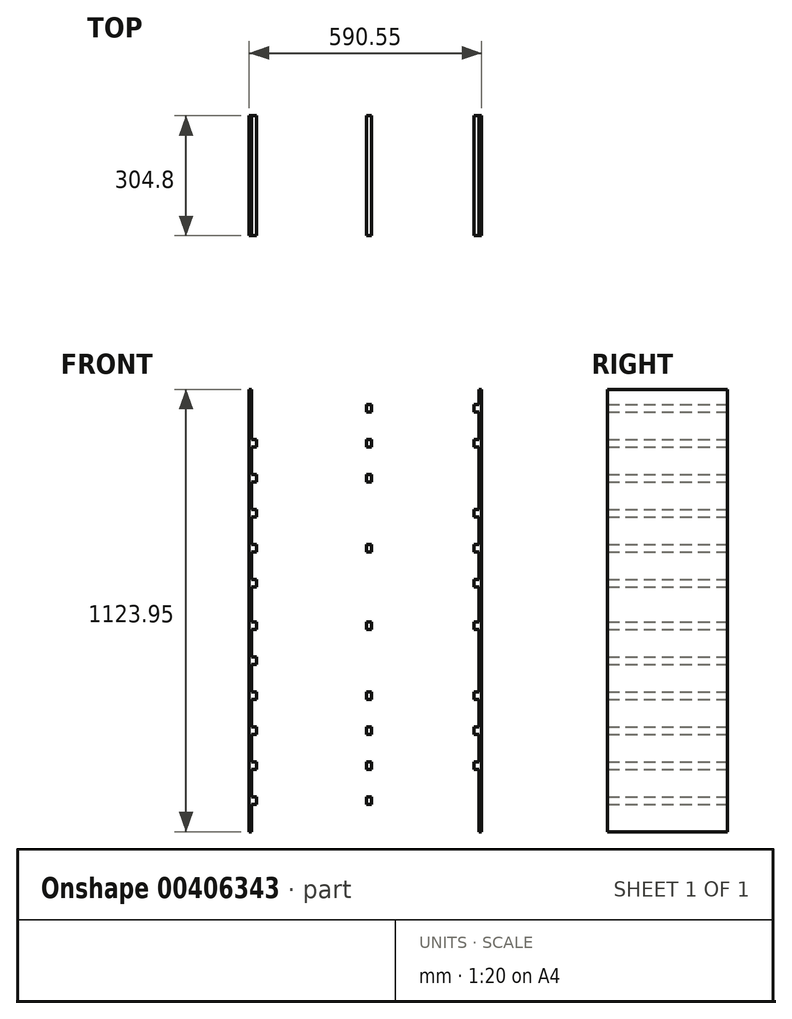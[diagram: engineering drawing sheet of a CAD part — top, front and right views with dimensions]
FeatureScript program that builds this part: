
annotation { "Feature Type Name" : "Feature", "Feature Type Description" : "" }
export const myFeature = defineFeature(function(context is Context, id is Id, definition is map)
    precondition{}
    {
        {
            var Q0;
            Q0=qCreatedBy(makeId("Front.planeOp"),FACE);
            var sketch = newSketch(context, id + "F0", { "sketchPlane" : qUnion([Q0])});
            skLineSegment(sketch, "E0.bottom", {"start": v(0, 0) * mm, "end": v(6.35, 0) * mm});
            skLineSegment(sketch, "E0.top", {"start": v(0, 1123.95) * mm, "end": v(6.35, 1123.95) * mm});
            skLineSegment(sketch, "E0.left", {"start": v(0, 0) * mm, "end": v(0, 1123.95) * mm});
            skLineSegment(sketch, "E0.right", {"start": v(6.35, 0) * mm, "end": v(6.35, 1123.95) * mm});
            skLineSegment(sketch, "E1.bottom", {"start": v(6.35, 0) * mm, "end": v(292.1, 0) * mm});
            skLineSegment(sketch, "E1.top", {"start": v(6.35, 19.05) * mm, "end": v(292.1, 19.05) * mm});
            skLineSegment(sketch, "E1.left", {"start": v(6.35, 0) * mm, "end": v(6.35, 19.05) * mm});
            skLineSegment(sketch, "E1.right", {"start": v(292.1, 0) * mm, "end": v(292.1, 19.05) * mm});
            skLineSegment(sketch, "E2.bottom", {"start": v(6.35, 69.85) * mm, "end": v(19.05, 69.85) * mm});
            skLineSegment(sketch, "E2.top", {"start": v(6.35, 88.9) * mm, "end": v(19.05, 88.9) * mm});
            skLineSegment(sketch, "E2.left", {"start": v(6.35, 69.85) * mm, "end": v(6.35, 88.9) * mm});
            skLineSegment(sketch, "E2.right", {"start": v(19.05, 69.85) * mm, "end": v(19.05, 88.9) * mm});
            skLineSegment(sketch, "E3.bottom", {"start": v(6.35, 158.75) * mm, "end": v(19.05, 158.75) * mm});
            skLineSegment(sketch, "E3.top", {"start": v(6.35, 177.8) * mm, "end": v(19.05, 177.8) * mm});
            skLineSegment(sketch, "E3.left", {"start": v(6.35, 158.75) * mm, "end": v(6.35, 177.8) * mm});
            skLineSegment(sketch, "E3.right", {"start": v(19.05, 158.75) * mm, "end": v(19.05, 177.8) * mm});
            skLineSegment(sketch, "E4.bottom", {"start": v(6.35, 247.65) * mm, "end": v(19.05, 247.65) * mm});
            skLineSegment(sketch, "E4.top", {"start": v(6.35, 266.7) * mm, "end": v(19.05, 266.7) * mm});
            skLineSegment(sketch, "E4.left", {"start": v(6.35, 247.65) * mm, "end": v(6.35, 266.7) * mm});
            skLineSegment(sketch, "E4.right", {"start": v(19.05, 247.65) * mm, "end": v(19.05, 266.7) * mm});
            skLineSegment(sketch, "E5.bottom", {"start": v(6.35, 336.55) * mm, "end": v(19.05, 336.55) * mm});
            skLineSegment(sketch, "E5.top", {"start": v(6.35, 355.6) * mm, "end": v(19.05, 355.6) * mm});
            skLineSegment(sketch, "E5.left", {"start": v(6.35, 336.55) * mm, "end": v(6.35, 355.6) * mm});
            skLineSegment(sketch, "E5.right", {"start": v(19.05, 336.55) * mm, "end": v(19.05, 355.6) * mm});
            skLineSegment(sketch, "E6.bottom", {"start": v(6.35, 425.45) * mm, "end": v(19.05, 425.45) * mm});
            skLineSegment(sketch, "E6.top", {"start": v(6.35, 444.5) * mm, "end": v(19.05, 444.5) * mm});
            skLineSegment(sketch, "E6.left", {"start": v(6.35, 425.45) * mm, "end": v(6.35, 444.5) * mm});
            skLineSegment(sketch, "E6.right", {"start": v(19.05, 425.45) * mm, "end": v(19.05, 444.5) * mm});
            skLineSegment(sketch, "E7.bottom", {"start": v(6.35, 514.35) * mm, "end": v(19.05, 514.35) * mm});
            skLineSegment(sketch, "E7.top", {"start": v(6.35, 533.4) * mm, "end": v(19.05, 533.4) * mm});
            skLineSegment(sketch, "E7.left", {"start": v(6.35, 514.35) * mm, "end": v(6.35, 533.4) * mm});
            skLineSegment(sketch, "E7.right", {"start": v(19.05, 514.35) * mm, "end": v(19.05, 533.4) * mm});
            skLineSegment(sketch, "E8.bottom", {"start": v(6.35, 571.5) * mm, "end": v(292.1, 571.5) * mm});
            skLineSegment(sketch, "E8.top", {"start": v(6.35, 552.45) * mm, "end": v(292.1, 552.45) * mm});
            skLineSegment(sketch, "E8.left", {"start": v(6.35, 571.5) * mm, "end": v(6.35, 552.45) * mm});
            skLineSegment(sketch, "E8.right", {"start": v(292.1, 571.5) * mm, "end": v(292.1, 552.45) * mm});
            skLineSegment(sketch, "E9.0.1.0", {"start": v(6.35, 1123.95) * mm, "end": v(292.1, 1123.95) * mm});
            skLineSegment(sketch, "E9.0.1.1", {"start": v(6.35, 1104.9) * mm, "end": v(292.1, 1104.9) * mm});
            skLineSegment(sketch, "E9.0.1.2", {"start": v(6.35, 908.05) * mm, "end": v(19.05, 908.05) * mm});
            skLineSegment(sketch, "E9.0.1.3", {"start": v(6.35, 819.15) * mm, "end": v(19.05, 819.15) * mm});
            skLineSegment(sketch, "E9.0.1.4", {"start": v(6.35, 1066.8) * mm, "end": v(6.35, 1085.85) * mm});
            skLineSegment(sketch, "E9.0.1.5", {"start": v(6.35, 622.3) * mm, "end": v(19.05, 622.3) * mm});
            skLineSegment(sketch, "E9.0.1.6", {"start": v(6.35, 641.35) * mm, "end": v(19.05, 641.35) * mm});
            skLineSegment(sketch, "E9.0.1.7", {"start": v(6.35, 622.3) * mm, "end": v(6.35, 641.35) * mm});
            skLineSegment(sketch, "E9.0.1.8", {"start": v(6.35, 977.9) * mm, "end": v(19.05, 977.9) * mm});
            skLineSegment(sketch, "E9.0.1.9", {"start": v(6.35, 1066.8) * mm, "end": v(19.05, 1066.8) * mm});
            skLineSegment(sketch, "E9.0.1.10", {"start": v(19.05, 622.3) * mm, "end": v(19.05, 641.35) * mm});
            skLineSegment(sketch, "E9.0.1.11", {"start": v(6.35, 711.2) * mm, "end": v(19.05, 711.2) * mm});
            skLineSegment(sketch, "E9.0.1.12", {"start": v(19.05, 977.9) * mm, "end": v(19.05, 996.95) * mm});
            skLineSegment(sketch, "E9.0.1.13", {"start": v(19.05, 889) * mm, "end": v(19.05, 908.05) * mm});
            skLineSegment(sketch, "E9.0.1.14", {"start": v(6.35, 889) * mm, "end": v(19.05, 889) * mm});
            skLineSegment(sketch, "E9.0.1.15", {"start": v(19.05, 711.2) * mm, "end": v(19.05, 730.25) * mm});
            skLineSegment(sketch, "E9.0.1.16", {"start": v(6.35, 1085.85) * mm, "end": v(19.05, 1085.85) * mm});
            skLineSegment(sketch, "E9.0.1.17", {"start": v(6.35, 800.1) * mm, "end": v(19.05, 800.1) * mm});
            skLineSegment(sketch, "E9.0.1.18", {"start": v(6.35, 730.25) * mm, "end": v(19.05, 730.25) * mm});
            skLineSegment(sketch, "E9.0.1.19", {"start": v(6.35, 711.2) * mm, "end": v(6.35, 730.25) * mm});
            skLineSegment(sketch, "E9.0.1.20", {"start": v(292.1, 1123.95) * mm, "end": v(292.1, 1104.9) * mm});
            skLineSegment(sketch, "E9.0.1.21", {"start": v(19.05, 800.1) * mm, "end": v(19.05, 819.15) * mm});
            skLineSegment(sketch, "E9.0.1.22", {"start": v(6.35, 977.9) * mm, "end": v(6.35, 996.95) * mm});
            skLineSegment(sketch, "E9.0.1.23", {"start": v(6.35, 996.95) * mm, "end": v(19.05, 996.95) * mm});
            skLineSegment(sketch, "E9.0.1.24", {"start": v(6.35, 889) * mm, "end": v(6.35, 908.05) * mm});
            skLineSegment(sketch, "E9.0.1.25", {"start": v(19.05, 1066.8) * mm, "end": v(19.05, 1085.85) * mm});
            skLineSegment(sketch, "E9.0.1.26", {"start": v(6.35, 800.1) * mm, "end": v(6.35, 819.15) * mm});
            skLineSegment(sketch, "E9.0.1.27", {"start": v(6.35, 1123.95) * mm, "end": v(6.35, 1104.9) * mm});
            skLineSegment(sketch, "E9.direction1", {"start": v(6.35, 69.85) * mm, "end": v(43.2, 69.85) * mm, "construction": true});
            skLineSegment(sketch, "E9.direction2", {"start": v(6.35, 69.85) * mm, "end": v(6.35, 622.3) * mm, "construction": true});
            skLineSegment(sketch, "E10.1.0.0", {"start": v(298.45, 1123.95) * mm, "end": v(584.2, 1123.95) * mm});
            skLineSegment(sketch, "E10.1.0.1", {"start": v(298.45, 1104.9) * mm, "end": v(584.2, 1104.9) * mm});
            skLineSegment(sketch, "E10.1.0.2", {"start": v(298.45, 0) * mm, "end": v(298.45, 1123.95) * mm});
            skLineSegment(sketch, "E10.1.0.3", {"start": v(292.1, 0) * mm, "end": v(292.1, 1123.95) * mm});
            skLineSegment(sketch, "E10.1.0.4", {"start": v(298.45, 0) * mm, "end": v(584.2, 0) * mm});
            skLineSegment(sketch, "E10.1.0.5", {"start": v(298.45, 19.05) * mm, "end": v(584.2, 19.05) * mm});
            skLineSegment(sketch, "E10.1.0.6", {"start": v(298.45, 571.5) * mm, "end": v(584.2, 571.5) * mm});
            skLineSegment(sketch, "E10.1.0.7", {"start": v(298.45, 69.85) * mm, "end": v(298.45, 622.3) * mm, "construction": true});
            skLineSegment(sketch, "E10.1.0.8", {"start": v(298.45, 552.45) * mm, "end": v(584.2, 552.45) * mm});
            skLineSegment(sketch, "E10.1.0.9", {"start": v(298.45, 69.85) * mm, "end": v(335.3, 69.85) * mm, "construction": true});
            skLineSegment(sketch, "E10.1.0.10", {"start": v(298.45, 425.45) * mm, "end": v(298.45, 444.5) * mm});
            skLineSegment(sketch, "E10.1.0.11", {"start": v(298.45, 1085.85) * mm, "end": v(311.15, 1085.85) * mm});
            skLineSegment(sketch, "E10.1.0.12", {"start": v(298.45, 1066.8) * mm, "end": v(311.15, 1066.8) * mm});
            skLineSegment(sketch, "E10.1.0.13", {"start": v(298.45, 177.8) * mm, "end": v(311.15, 177.8) * mm});
            skLineSegment(sketch, "E10.1.0.14", {"start": v(298.45, 908.05) * mm, "end": v(311.15, 908.05) * mm});
            skLineSegment(sketch, "E10.1.0.15", {"start": v(298.45, 158.75) * mm, "end": v(298.45, 177.8) * mm});
            skLineSegment(sketch, "E10.1.0.16", {"start": v(311.15, 514.35) * mm, "end": v(311.15, 533.4) * mm});
            skLineSegment(sketch, "E10.1.0.17", {"start": v(311.15, 1066.8) * mm, "end": v(311.15, 1085.85) * mm});
            skLineSegment(sketch, "E10.1.0.18", {"start": v(311.15, 425.45) * mm, "end": v(311.15, 444.5) * mm});
            skLineSegment(sketch, "E10.1.0.19", {"start": v(298.45, 336.55) * mm, "end": v(311.15, 336.55) * mm});
            skLineSegment(sketch, "E10.1.0.20", {"start": v(298.45, 622.3) * mm, "end": v(298.45, 641.35) * mm});
            skLineSegment(sketch, "E10.1.0.21", {"start": v(298.45, 996.95) * mm, "end": v(311.15, 996.95) * mm});
            skLineSegment(sketch, "E10.1.0.22", {"start": v(298.45, 514.35) * mm, "end": v(298.45, 533.4) * mm});
            skLineSegment(sketch, "E10.1.0.23", {"start": v(311.15, 158.75) * mm, "end": v(311.15, 177.8) * mm});
            skLineSegment(sketch, "E10.1.0.24", {"start": v(311.15, 711.2) * mm, "end": v(311.15, 730.25) * mm});
            skLineSegment(sketch, "E10.1.0.25", {"start": v(584.2, 571.5) * mm, "end": v(584.2, 552.45) * mm});
            skLineSegment(sketch, "E10.1.0.26", {"start": v(298.45, 711.2) * mm, "end": v(311.15, 711.2) * mm});
            skLineSegment(sketch, "E10.1.0.27", {"start": v(298.45, 1123.95) * mm, "end": v(298.45, 1104.9) * mm});
            skLineSegment(sketch, "E10.1.0.28", {"start": v(298.45, 730.25) * mm, "end": v(311.15, 730.25) * mm});
            skLineSegment(sketch, "E10.1.0.29", {"start": v(298.45, 889) * mm, "end": v(298.45, 908.05) * mm});
            skLineSegment(sketch, "E10.1.0.30", {"start": v(298.45, 977.9) * mm, "end": v(311.15, 977.9) * mm});
            skLineSegment(sketch, "E10.1.0.31", {"start": v(298.45, 355.6) * mm, "end": v(311.15, 355.6) * mm});
            skLineSegment(sketch, "E10.1.0.32", {"start": v(298.45, 336.55) * mm, "end": v(298.45, 355.6) * mm});
            skLineSegment(sketch, "E10.1.0.33", {"start": v(311.15, 622.3) * mm, "end": v(311.15, 641.35) * mm});
            skLineSegment(sketch, "E10.1.0.34", {"start": v(298.45, 514.35) * mm, "end": v(311.15, 514.35) * mm});
            skLineSegment(sketch, "E10.1.0.35", {"start": v(298.45, 800.1) * mm, "end": v(298.45, 819.15) * mm});
            skLineSegment(sketch, "E10.1.0.36", {"start": v(298.45, 800.1) * mm, "end": v(311.15, 800.1) * mm});
            skLineSegment(sketch, "E10.1.0.37", {"start": v(298.45, 641.35) * mm, "end": v(311.15, 641.35) * mm});
            skLineSegment(sketch, "E10.1.0.38", {"start": v(298.45, 977.9) * mm, "end": v(298.45, 996.95) * mm});
            skLineSegment(sketch, "E10.1.0.39", {"start": v(584.2, 0) * mm, "end": v(584.2, 19.05) * mm});
            skLineSegment(sketch, "E10.1.0.40", {"start": v(298.45, 88.9) * mm, "end": v(311.15, 88.9) * mm});
            skLineSegment(sketch, "E10.1.0.41", {"start": v(298.45, 69.85) * mm, "end": v(298.45, 88.9) * mm});
            skLineSegment(sketch, "E10.1.0.42", {"start": v(311.15, 69.85) * mm, "end": v(311.15, 88.9) * mm});
            skLineSegment(sketch, "E10.1.0.43", {"start": v(298.45, 158.75) * mm, "end": v(311.15, 158.75) * mm});
            skLineSegment(sketch, "E10.1.0.44", {"start": v(298.45, 711.2) * mm, "end": v(298.45, 730.25) * mm});
            skLineSegment(sketch, "E10.1.0.45", {"start": v(298.45, 819.15) * mm, "end": v(311.15, 819.15) * mm});
            skLineSegment(sketch, "E10.1.0.46", {"start": v(311.15, 336.55) * mm, "end": v(311.15, 355.6) * mm});
            skLineSegment(sketch, "E10.1.0.47", {"start": v(298.45, 247.65) * mm, "end": v(311.15, 247.65) * mm});
            skLineSegment(sketch, "E10.1.0.48", {"start": v(311.15, 977.9) * mm, "end": v(311.15, 996.95) * mm});
            skLineSegment(sketch, "E10.1.0.49", {"start": v(584.2, 1123.95) * mm, "end": v(584.2, 1104.9) * mm});
            skLineSegment(sketch, "E10.1.0.50", {"start": v(298.45, 1066.8) * mm, "end": v(298.45, 1085.85) * mm});
            skLineSegment(sketch, "E10.1.0.51", {"start": v(298.45, 425.45) * mm, "end": v(311.15, 425.45) * mm});
            skLineSegment(sketch, "E10.1.0.52", {"start": v(311.15, 889) * mm, "end": v(311.15, 908.05) * mm});
            skLineSegment(sketch, "E10.1.0.53", {"start": v(311.15, 800.1) * mm, "end": v(311.15, 819.15) * mm});
            skLineSegment(sketch, "E10.1.0.54", {"start": v(298.45, 444.5) * mm, "end": v(311.15, 444.5) * mm});
            skLineSegment(sketch, "E10.1.0.55", {"start": v(298.45, 247.65) * mm, "end": v(298.45, 266.7) * mm});
            skLineSegment(sketch, "E10.1.0.56", {"start": v(298.45, 889) * mm, "end": v(311.15, 889) * mm});
            skLineSegment(sketch, "E10.1.0.57", {"start": v(298.45, 571.5) * mm, "end": v(298.45, 552.45) * mm});
            skLineSegment(sketch, "E10.1.0.58", {"start": v(311.15, 247.65) * mm, "end": v(311.15, 266.7) * mm});
            skLineSegment(sketch, "E10.1.0.59", {"start": v(298.45, 266.7) * mm, "end": v(311.15, 266.7) * mm});
            skLineSegment(sketch, "E10.1.0.60", {"start": v(298.45, 622.3) * mm, "end": v(311.15, 622.3) * mm});
            skLineSegment(sketch, "E10.1.0.61", {"start": v(298.45, 533.4) * mm, "end": v(311.15, 533.4) * mm});
            skLineSegment(sketch, "E10.1.0.62", {"start": v(292.1, 0) * mm, "end": v(298.45, 0) * mm});
            skLineSegment(sketch, "E10.1.0.63", {"start": v(292.1, 1123.95) * mm, "end": v(298.45, 1123.95) * mm});
            skLineSegment(sketch, "E10.1.0.64", {"start": v(298.45, 0) * mm, "end": v(298.45, 19.05) * mm});
            skLineSegment(sketch, "E10.1.0.65", {"start": v(298.45, 69.85) * mm, "end": v(311.15, 69.85) * mm});
            skLineSegment(sketch, "E10.direction1", {"start": v(0, 0) * mm, "end": v(292.1, 0) * mm, "construction": true});
            skLineSegment(sketch, "E11.bottom", {"start": v(584.2, 0) * mm, "end": v(590.55, 0) * mm});
            skLineSegment(sketch, "E11.top", {"start": v(584.2, 1123.95) * mm, "end": v(590.55, 1123.95) * mm});
            skLineSegment(sketch, "E11.left", {"start": v(584.2, 0) * mm, "end": v(584.2, 1123.95) * mm});
            skLineSegment(sketch, "E11.right", {"start": v(590.55, 0) * mm, "end": v(590.55, 1123.95) * mm});
            skLineSegment(sketch, "E12.1.0.0", {"start": v(584.2, 69.85) * mm, "end": v(584.2, 88.9) * mm});
            skLineSegment(sketch, "E12.1.0.1", {"start": v(571.5, 69.85) * mm, "end": v(571.5, 622.3) * mm, "construction": true});
            skLineSegment(sketch, "E12.1.0.2", {"start": v(571.5, 336.55) * mm, "end": v(571.5, 355.6) * mm});
            skLineSegment(sketch, "E12.1.0.3", {"start": v(571.5, 336.55) * mm, "end": v(584.2, 336.55) * mm});
            skLineSegment(sketch, "E12.1.0.4", {"start": v(571.5, 977.9) * mm, "end": v(584.2, 977.9) * mm});
            skLineSegment(sketch, "E12.1.0.5", {"start": v(584.2, 336.55) * mm, "end": v(584.2, 355.6) * mm});
            skLineSegment(sketch, "E12.1.0.6", {"start": v(571.5, 514.35) * mm, "end": v(584.2, 514.35) * mm});
            skLineSegment(sketch, "E12.1.0.7", {"start": v(571.5, 1066.8) * mm, "end": v(571.5, 1085.85) * mm});
            skLineSegment(sketch, "E12.1.0.8", {"start": v(584.2, 425.45) * mm, "end": v(584.2, 444.5) * mm});
            skLineSegment(sketch, "E12.1.0.9", {"start": v(571.5, 800.1) * mm, "end": v(571.5, 819.15) * mm});
            skLineSegment(sketch, "E12.1.0.10", {"start": v(571.5, 425.45) * mm, "end": v(584.2, 425.45) * mm});
            skLineSegment(sketch, "E12.1.0.11", {"start": v(584.2, 977.9) * mm, "end": v(584.2, 996.95) * mm});
            skLineSegment(sketch, "E12.1.0.12", {"start": v(584.2, 889) * mm, "end": v(584.2, 908.05) * mm});
            skLineSegment(sketch, "E12.1.0.13", {"start": v(571.5, 800.1) * mm, "end": v(584.2, 800.1) * mm});
            skLineSegment(sketch, "E12.1.0.14", {"start": v(571.5, 908.05) * mm, "end": v(584.2, 908.05) * mm});
            skLineSegment(sketch, "E12.1.0.15", {"start": v(584.2, 800.1) * mm, "end": v(584.2, 819.15) * mm});
            skLineSegment(sketch, "E12.1.0.16", {"start": v(571.5, 641.35) * mm, "end": v(584.2, 641.35) * mm});
            skLineSegment(sketch, "E12.1.0.17", {"start": v(571.5, 996.95) * mm, "end": v(584.2, 996.95) * mm});
            skLineSegment(sketch, "E12.1.0.18", {"start": v(584.2, 1066.8) * mm, "end": v(584.2, 1085.85) * mm});
            skLineSegment(sketch, "E12.1.0.19", {"start": v(565.15, 571.5) * mm, "end": v(565.15, 552.45) * mm});
            skLineSegment(sketch, "E12.1.0.20", {"start": v(584.2, 622.3) * mm, "end": v(584.2, 641.35) * mm});
            skLineSegment(sketch, "E12.1.0.21", {"start": v(571.5, 889) * mm, "end": v(571.5, 908.05) * mm});
            skLineSegment(sketch, "E12.1.0.22", {"start": v(571.5, 819.15) * mm, "end": v(584.2, 819.15) * mm});
            skLineSegment(sketch, "E12.1.0.23", {"start": v(571.5, 533.4) * mm, "end": v(584.2, 533.4) * mm});
            skLineSegment(sketch, "E12.1.0.24", {"start": v(571.5, 177.8) * mm, "end": v(584.2, 177.8) * mm});
            skLineSegment(sketch, "E12.1.0.25", {"start": v(571.5, 730.25) * mm, "end": v(584.2, 730.25) * mm});
            skLineSegment(sketch, "E12.1.0.26", {"start": v(571.5, 711.2) * mm, "end": v(571.5, 730.25) * mm});
            skLineSegment(sketch, "E12.1.0.27", {"start": v(571.5, 444.5) * mm, "end": v(584.2, 444.5) * mm});
            skLineSegment(sketch, "E12.1.0.28", {"start": v(571.5, 977.9) * mm, "end": v(571.5, 996.95) * mm});
            skLineSegment(sketch, "E12.1.0.29", {"start": v(571.5, 514.35) * mm, "end": v(571.5, 533.4) * mm});
            skLineSegment(sketch, "E12.1.0.30", {"start": v(571.5, 247.65) * mm, "end": v(571.5, 266.7) * mm});
            skLineSegment(sketch, "E12.1.0.31", {"start": v(584.2, 158.75) * mm, "end": v(584.2, 177.8) * mm});
            skLineSegment(sketch, "E12.1.0.32", {"start": v(571.5, 158.75) * mm, "end": v(571.5, 177.8) * mm});
            skLineSegment(sketch, "E12.1.0.33", {"start": v(571.5, 889) * mm, "end": v(584.2, 889) * mm});
            skLineSegment(sketch, "E12.1.0.34", {"start": v(571.5, 88.9) * mm, "end": v(584.2, 88.9) * mm});
            skLineSegment(sketch, "E12.1.0.35", {"start": v(584.2, 711.2) * mm, "end": v(584.2, 730.25) * mm});
            skLineSegment(sketch, "E12.1.0.36", {"start": v(571.5, 247.65) * mm, "end": v(584.2, 247.65) * mm});
            skLineSegment(sketch, "E12.1.0.37", {"start": v(571.5, 355.6) * mm, "end": v(584.2, 355.6) * mm});
            skLineSegment(sketch, "E12.1.0.38", {"start": v(571.5, 571.5) * mm, "end": v(571.5, 552.45) * mm});
            skLineSegment(sketch, "E12.1.0.39", {"start": v(571.5, 69.85) * mm, "end": v(571.5, 88.9) * mm});
            skLineSegment(sketch, "E12.1.0.40", {"start": v(571.5, 1085.85) * mm, "end": v(584.2, 1085.85) * mm});
            skLineSegment(sketch, "E12.1.0.41", {"start": v(571.5, 266.7) * mm, "end": v(584.2, 266.7) * mm});
            skLineSegment(sketch, "E12.1.0.42", {"start": v(571.5, 158.75) * mm, "end": v(584.2, 158.75) * mm});
            skLineSegment(sketch, "E12.1.0.43", {"start": v(584.2, 247.65) * mm, "end": v(584.2, 266.7) * mm});
            skLineSegment(sketch, "E12.1.0.44", {"start": v(584.2, 514.35) * mm, "end": v(584.2, 533.4) * mm});
            skLineSegment(sketch, "E12.1.0.45", {"start": v(571.5, 711.2) * mm, "end": v(584.2, 711.2) * mm});
            skLineSegment(sketch, "E12.1.0.46", {"start": v(571.5, 425.45) * mm, "end": v(571.5, 444.5) * mm});
            skLineSegment(sketch, "E12.1.0.47", {"start": v(571.5, 1066.8) * mm, "end": v(584.2, 1066.8) * mm});
            skLineSegment(sketch, "E12.1.0.48", {"start": v(571.5, 622.3) * mm, "end": v(571.5, 641.35) * mm});
            skLineSegment(sketch, "E12.1.0.49", {"start": v(571.5, 622.3) * mm, "end": v(584.2, 622.3) * mm});
            skLineSegment(sketch, "E12.1.0.50", {"start": v(571.5, 69.85) * mm, "end": v(584.2, 69.85) * mm});
            skLineSegment(sketch, "E12.direction1", {"start": v(298.45, 69.85) * mm, "end": v(571.5, 69.85) * mm, "construction": true});
            skSolve(sketch);
        }
        {
            var Q0;
            Q0=makeQuery(id+"F0.imprint","IMPRINT",FACE,{"disambiguationData":[TD([[makeQuery(id+"F0.imprint","IMPRINT",EDGE,{"derivedFrom":sQuery(id+"F0.wireOp",EDGE,"E2.bottom")}),1.0]])]});
            var Q1;
            Q1=makeQuery(id+"F0.imprint","IMPRINT",FACE,{"disambiguationData":[TD([[makeQuery(id+"F0.imprint","IMPRINT",EDGE,{"derivedFrom":sQuery(id+"F0.wireOp",EDGE,"E3.bottom")}),1.0]])]});
            var Q2;
            Q2=makeQuery(id+"F0.imprint","IMPRINT",FACE,{"disambiguationData":[TD([[makeQuery(id+"F0.imprint","IMPRINT",EDGE,{"derivedFrom":sQuery(id+"F0.wireOp",EDGE,"E4.bottom")}),1.0]])]});
            var Q3;
            Q3=makeQuery(id+"F0.imprint","IMPRINT",FACE,{"disambiguationData":[TD([[makeQuery(id+"F0.imprint","IMPRINT",EDGE,{"derivedFrom":sQuery(id+"F0.wireOp",EDGE,"E5.bottom")}),1.0]])]});
            var Q4;
            Q4=makeQuery(id+"F0.imprint","IMPRINT",FACE,{"disambiguationData":[TD([[makeQuery(id+"F0.imprint","IMPRINT",EDGE,{"derivedFrom":sQuery(id+"F0.wireOp",EDGE,"E6.bottom")}),1.0]])]});
            var Q5;
            Q5=makeQuery(id+"F0.imprint","IMPRINT",FACE,{"disambiguationData":[TD([[makeQuery(id+"F0.imprint","IMPRINT",EDGE,{"derivedFrom":sQuery(id+"F0.wireOp",EDGE,"E7.bottom")}),1.0]])]});
            var Q6;
            Q6=makeQuery(id+"F0.imprint","IMPRINT",FACE,{"disambiguationData":[TD([[makeQuery(id+"F0.imprint","IMPRINT",EDGE,{"derivedFrom":sQuery(id+"F0.wireOp",EDGE,"E9.0.1.2")}),-1.0]])]});
            var Q7;
            Q7=makeQuery(id+"F0.imprint","IMPRINT",FACE,{"disambiguationData":[TD([[makeQuery(id+"F0.imprint","IMPRINT",EDGE,{"derivedFrom":sQuery(id+"F0.wireOp",EDGE,"E9.0.1.3")}),-1.0]])]});
            var Q8;
            Q8=makeQuery(id+"F0.imprint","IMPRINT",FACE,{"disambiguationData":[TD([[makeQuery(id+"F0.imprint","IMPRINT",EDGE,{"derivedFrom":sQuery(id+"F0.wireOp",EDGE,"E9.0.1.4")}),-1.0]])]});
            var Q9;
            Q9=makeQuery(id+"F0.imprint","IMPRINT",FACE,{"disambiguationData":[TD([[makeQuery(id+"F0.imprint","IMPRINT",EDGE,{"derivedFrom":sQuery(id+"F0.wireOp",EDGE,"E9.0.1.5")}),1.0]])]});
            var Q10;
            Q10=makeQuery(id+"F0.imprint","IMPRINT",FACE,{"disambiguationData":[TD([[makeQuery(id+"F0.imprint","IMPRINT",EDGE,{"derivedFrom":sQuery(id+"F0.wireOp",EDGE,"E9.0.1.8")}),1.0]])]});
            var Q11;
            Q11=makeQuery(id+"F0.imprint","IMPRINT",FACE,{"disambiguationData":[TD([[makeQuery(id+"F0.imprint","IMPRINT",EDGE,{"derivedFrom":sQuery(id+"F0.wireOp",EDGE,"E9.0.1.11")}),1.0]])]});
            var Q12;
            Q12=makeQuery(id+"F0.imprint","IMPRINT",FACE,{"disambiguationData":[TD([[makeQuery(id+"F0.imprint","IMPRINT",EDGE,{"derivedFrom":sQuery(id+"F0.wireOp",EDGE,"E12.1.0.9")}),-1.0]])]});
            var Q13;
            Q13=makeQuery(id+"F0.imprint","IMPRINT",FACE,{"disambiguationData":[TD([[makeQuery(id+"F0.imprint","IMPRINT",EDGE,{"derivedFrom":sQuery(id+"F0.wireOp",EDGE,"E10.1.0.35")}),-1.0]])]});
            var Q14;
            Q14=makeQuery(id+"F0.imprint","IMPRINT",FACE,{"disambiguationData":[TD([[makeQuery(id+"F0.imprint","IMPRINT",EDGE,{"derivedFrom":sQuery(id+"F0.wireOp",EDGE,"E12.1.0.7")}),-1.0]])]});
            var Q15;
            Q15=makeQuery(id+"F0.imprint","IMPRINT",FACE,{"disambiguationData":[TD([[makeQuery(id+"F0.imprint","IMPRINT",EDGE,{"derivedFrom":sQuery(id+"F0.wireOp",EDGE,"E10.1.0.14")}),-1.0]])]});
            var Q16;
            Q16=makeQuery(id+"F0.imprint","IMPRINT",FACE,{"disambiguationData":[TD([[makeQuery(id+"F0.imprint","IMPRINT",EDGE,{"derivedFrom":sQuery(id+"F0.wireOp",EDGE,"E10.1.0.11")}),-1.0]])]});
            var Q17;
            Q17=makeQuery(id+"F0.imprint","IMPRINT",FACE,{"disambiguationData":[TD([[makeQuery(id+"F0.imprint","IMPRINT",EDGE,{"derivedFrom":sQuery(id+"F0.wireOp",EDGE,"E12.1.0.16")}),-1.0]])]});
            var Q18;
            Q18=makeQuery(id+"F0.imprint","IMPRINT",FACE,{"disambiguationData":[TD([[makeQuery(id+"F0.imprint","IMPRINT",EDGE,{"derivedFrom":sQuery(id+"F0.wireOp",EDGE,"E12.1.0.12")}),1.0]])]});
            var Q19;
            Q19=makeQuery(id+"F0.imprint","IMPRINT",FACE,{"disambiguationData":[TD([[makeQuery(id+"F0.imprint","IMPRINT",EDGE,{"derivedFrom":sQuery(id+"F0.wireOp",EDGE,"E10.1.0.24")}),1.0]])]});
            var Q20;
            Q20=makeQuery(id+"F0.imprint","IMPRINT",FACE,{"disambiguationData":[TD([[makeQuery(id+"F0.imprint","IMPRINT",EDGE,{"derivedFrom":sQuery(id+"F0.wireOp",EDGE,"E10.1.0.21")}),-1.0]])]});
            var Q21;
            Q21=makeQuery(id+"F0.imprint","IMPRINT",FACE,{"disambiguationData":[TD([[makeQuery(id+"F0.imprint","IMPRINT",EDGE,{"derivedFrom":sQuery(id+"F0.wireOp",EDGE,"E12.1.0.25")}),-1.0]])]});
            var Q22;
            Q22=makeQuery(id+"F0.imprint","IMPRINT",FACE,{"disambiguationData":[TD([[makeQuery(id+"F0.imprint","IMPRINT",EDGE,{"derivedFrom":sQuery(id+"F0.wireOp",EDGE,"E12.1.0.4")}),1.0]])]});
            var Q23;
            Q23=makeQuery(id+"F0.imprint","IMPRINT",FACE,{"disambiguationData":[TD([[makeQuery(id+"F0.imprint","IMPRINT",EDGE,{"derivedFrom":sQuery(id+"F0.wireOp",EDGE,"E10.1.0.20")}),-1.0]])]});
            var Q24;
            Q24=makeQuery(id+"F0.imprint","IMPRINT",FACE,{"disambiguationData":[TD([[makeQuery(id+"F0.imprint","IMPRINT",EDGE,{"derivedFrom":sQuery(id+"F0.wireOp",EDGE,"E12.1.0.8")}),1.0]])]});
            var Q25;
            Q25=makeQuery(id+"F0.imprint","IMPRINT",FACE,{"disambiguationData":[TD([[makeQuery(id+"F0.imprint","IMPRINT",EDGE,{"derivedFrom":sQuery(id+"F0.wireOp",EDGE,"E10.1.0.16")}),1.0]])]});
            var Q26;
            Q26=makeQuery(id+"F0.imprint","IMPRINT",FACE,{"disambiguationData":[TD([[makeQuery(id+"F0.imprint","IMPRINT",EDGE,{"derivedFrom":sQuery(id+"F0.wireOp",EDGE,"E10.1.0.19")}),1.0]])]});
            var Q27;
            Q27=makeQuery(id+"F0.imprint","IMPRINT",FACE,{"disambiguationData":[TD([[makeQuery(id+"F0.imprint","IMPRINT",EDGE,{"derivedFrom":sQuery(id+"F0.wireOp",EDGE,"E12.1.0.24")}),-1.0]])]});
            var Q28;
            Q28=makeQuery(id+"F0.imprint","IMPRINT",FACE,{"disambiguationData":[TD([[makeQuery(id+"F0.imprint","IMPRINT",EDGE,{"derivedFrom":sQuery(id+"F0.wireOp",EDGE,"E12.1.0.30")}),-1.0]])]});
            var Q29;
            Q29=makeQuery(id+"F0.imprint","IMPRINT",FACE,{"disambiguationData":[TD([[makeQuery(id+"F0.imprint","IMPRINT",EDGE,{"derivedFrom":sQuery(id+"F0.wireOp",EDGE,"E10.1.0.13")}),-1.0]])]});
            var Q30;
            Q30=makeQuery(id+"F0.imprint","IMPRINT",FACE,{"disambiguationData":[TD([[makeQuery(id+"F0.imprint","IMPRINT",EDGE,{"derivedFrom":sQuery(id+"F0.wireOp",EDGE,"E10.1.0.47")}),1.0]])]});
            var Q31;
            Q31=makeQuery(id+"F0.imprint","IMPRINT",FACE,{"disambiguationData":[TD([[makeQuery(id+"F0.imprint","IMPRINT",EDGE,{"derivedFrom":sQuery(id+"F0.wireOp",EDGE,"E12.1.0.6")}),1.0]])]});
            var Q32;
            Q32=makeQuery(id+"F0.imprint","IMPRINT",FACE,{"disambiguationData":[TD([[makeQuery(id+"F0.imprint","IMPRINT",EDGE,{"derivedFrom":sQuery(id+"F0.wireOp",EDGE,"E10.1.0.40")}),-1.0]])]});
            var Q33;
            Q33=makeQuery(id+"F0.imprint","IMPRINT",FACE,{"disambiguationData":[TD([[makeQuery(id+"F0.imprint","IMPRINT",EDGE,{"derivedFrom":sQuery(id+"F0.wireOp",EDGE,"E10.1.0.10")}),-1.0]])]});
            var Q34;
            Q34=makeQuery(id+"F0.imprint","IMPRINT",FACE,{"disambiguationData":[TD([[makeQuery(id+"F0.imprint","IMPRINT",EDGE,{"derivedFrom":sQuery(id+"F0.wireOp",EDGE,"E12.1.0.0")}),1.0]])]});
            var Q35;
            Q35=makeQuery(id+"F0.imprint","IMPRINT",FACE,{"disambiguationData":[TD([[makeQuery(id+"F0.imprint","IMPRINT",EDGE,{"derivedFrom":sQuery(id+"F0.wireOp",EDGE,"E12.1.0.2")}),-1.0]])]});
            var Q36;
            Q36=makeQuery(id+"F0.imprint","IMPRINT",FACE,{"disambiguationData":[TD([[makeQuery(id+"F0.imprint","IMPRINT",EDGE,{"derivedFrom":sQuery(id+"F0.wireOp",EDGE,"E0.bottom")}),1.0]])]});
            var Q37;
            {var subQ20=sQuery(id+"F0.wireOp",EDGE,"E10.1.0.10");Q37=makeQuery(id+"F0.imprint","IMPRINT",FACE,{"disambiguationData":[TD([[makeQuery(id+"F0.imprint","IMPRINT",EDGE,{"derivedFrom":subQ20}),1.0]])]});}
            var Q38;
            {var subQ16=sQuery(id+"F0.wireOp",EDGE,"E11.bottom");Q38=makeQuery(id+"F0.imprint","IMPRINT",FACE,{"disambiguationData":[TD([[makeQuery(id+"F0.imprint","IMPRINT",EDGE,{"derivedFrom":subQ16}),1.0]])]});}
            extrude(context, id + "F1", {"entities" : qUnion([Q0, Q1, Q2, Q3, Q4, Q5, Q6, Q7, Q8, Q9, Q10, Q11, Q12, Q13, Q14, Q15, Q16, Q17, Q18, Q19, Q20, Q21, Q22, Q23, Q24, Q25, Q26, Q27, Q28, Q29, Q30, Q31, Q32, Q33, Q34, Q35, Q36, Q37, Q38]), "depth" : 304.8 * mm});
        }
    });
